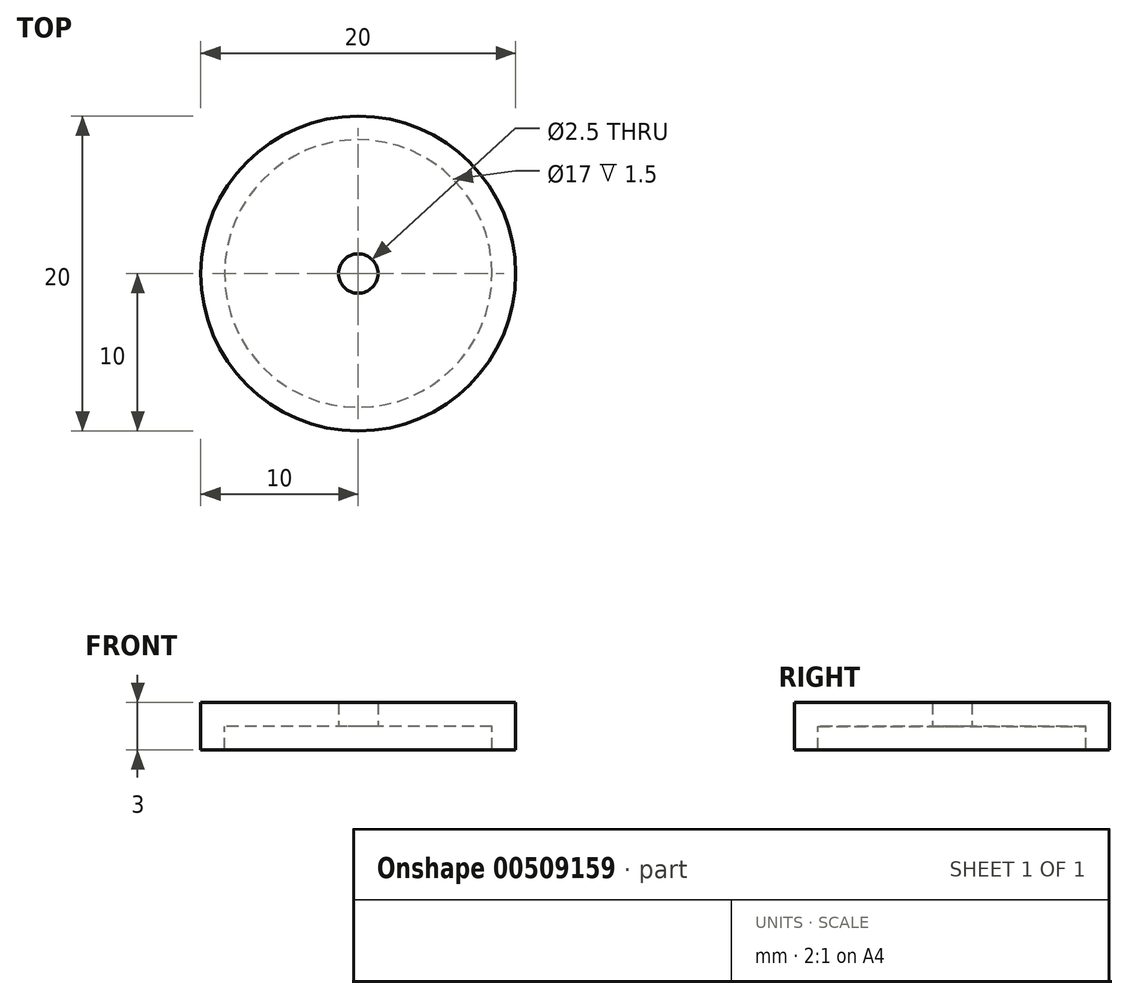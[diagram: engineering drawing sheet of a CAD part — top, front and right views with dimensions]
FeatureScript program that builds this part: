
annotation { "Feature Type Name" : "Feature", "Feature Type Description" : "" }
export const myFeature = defineFeature(function(context is Context, id is Id, definition is map)
    precondition{}
    {
        {
            var Q0;
            Q0=qCreatedBy(makeId("Top.planeOp"),FACE);
            cPlane(context, id + "F0", {"entities" : qUnion([Q0]), "cplaneType" : CPlaneType.OFFSET, "offset" : 10 * mm, "width" : 150 * mm, "height" : 150 * mm});
        }
        {
            var Q0;
            Q0=qCreatedBy(id+"F0.planeOp",FACE);
            var sketch = newSketch(context, id + "F1", { "sketchPlane" : qUnion([Q0])});
            skCircle(sketch, "E0", {"center": v(0, 0) * mm, "radius": 8.5 * mm});
            skCircle(sketch, "E1", {"center": v(0, 0) * mm, "radius": 10 * mm});
            skCircle(sketch, "E2", {"center": v(0, 0) * mm, "radius": 1.25 * mm});
            skSolve(sketch);
        }
        {
            var Q0;
            Q0=makeQuery(id+"F1.imprint","IMPRINT",FACE,{"disambiguationData":[TD([[makeQuery(id+"F1.imprint","IMPRINT",EDGE,{"derivedFrom":sQuery(id+"F1.wireOp",EDGE,"E0")}),1.0]])]});
            var Q1;
            Q1=makeQuery(id+"F1.imprint","IMPRINT",FACE,{"disambiguationData":[TD([[makeQuery(id+"F1.imprint","IMPRINT",EDGE,{"derivedFrom":sQuery(id+"F1.wireOp",EDGE,"E0")}),-1.0]])]});
            extrude(context, id + "F2", {"entities" : qUnion([Q0, Q1]), "depth" : 1.5 * mm});
        }
        {
            var Q0;
            Q0=makeQuery(id+"F1.imprint","IMPRINT",FACE,{"disambiguationData":[TD([[makeQuery(id+"F1.imprint","IMPRINT",EDGE,{"derivedFrom":sQuery(id+"F1.wireOp",EDGE,"E0")}),-1.0]])]});
            extrude(context, id + "F3", {"entities" : qUnion([Q0]), "operationType" : NewBodyOperationType.ADD, "oppositeDirection" : true, "depth" : 1.5 * mm});
        }
    });
